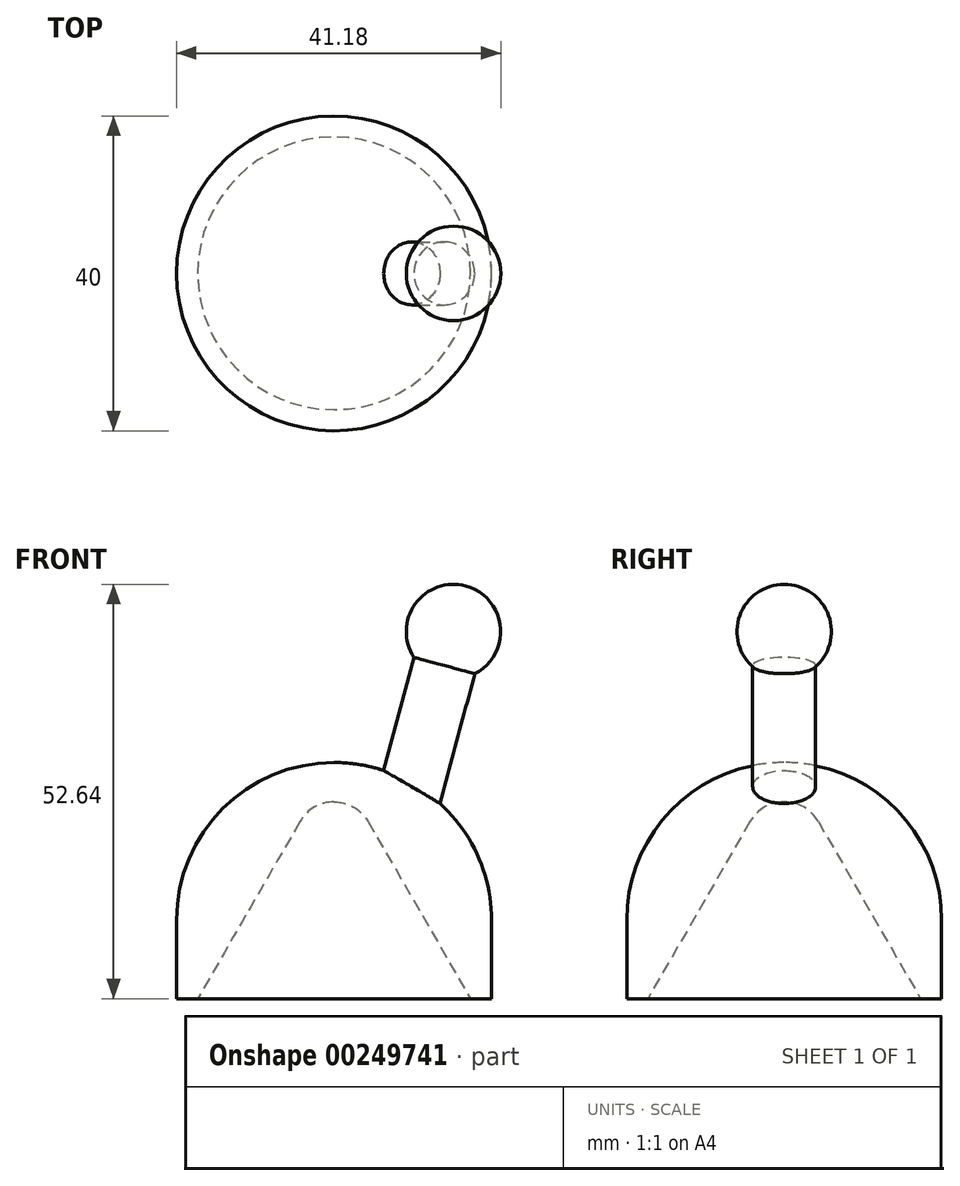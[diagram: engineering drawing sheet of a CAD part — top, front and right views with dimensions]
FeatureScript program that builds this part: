
annotation { "Feature Type Name" : "Feature", "Feature Type Description" : "" }
export const myFeature = defineFeature(function(context is Context, id is Id, definition is map)
    precondition{}
    {
        {
            var Q0;
            Q0=qCreatedBy(makeId("Front.planeOp"),FACE);
            var sketch = newSketch(context, id + "F0", { "sketchPlane" : qUnion([Q0])});
            skArc(sketch, "E0", {"start": v(4.33, 22.5) * mm, "mid": v(2.5, 24.33) * mm, "end": v(0, 25) * mm});
            skLineSegment(sketch, "E1", {"start": v(4.33, 22.5) * mm, "end": v(17.32, 0) * mm});
            skLineSegment(sketch, "E2", {"start": v(17.32, 0) * mm, "end": v(20, 0) * mm});
            skLineSegment(sketch, "E3", {"start": v(20, 0) * mm, "end": v(20, 10) * mm});
            skLineSegment(sketch, "E4", {"start": v(0, 0) * mm, "end": v(0, 30) * mm, "construction": true});
            skArc(sketch, "E5", {"start": v(20, 10) * mm, "mid": v(14.14, 24.14) * mm, "end": v(0, 30) * mm});
            skLineSegment(sketch, "E6", {"start": v(0, 25) * mm, "end": v(0, 30) * mm});
            skSolve(sketch);
        }
        {
            var Q0;
            Q0=makeQuery(id+"F0.imprint","IMPRINT",FACE,{"disambiguationData":[TD([[makeQuery(id+"F0.imprint","IMPRINT",EDGE,{"derivedFrom":sQuery(id+"F0.wireOp",EDGE,"E0")}),-1.0]])]});
            var Q1;
            Q1=sQuery(id+"F0.wireOp",EDGE,"E4");
            revolve(context, id + "F1", {"entities" : qUnion([Q0]), "axis" : qUnion([Q1]), "revolveType" : RevolveType.FULL});
        }
        {
            var Q0;
            Q0=qCreatedBy(makeId("Front.planeOp"),FACE);
            var sketch = newSketch(context, id + "F2", { "sketchPlane" : qUnion([Q0])});
            skArc(sketch, "E7", {"start": v(20, 10) * mm, "mid": v(0, 30) * mm, "end": v(-20, 10) * mm, "construction": true});
            skLineSegment(sketch, "E8", {"start": v(2.68, 0) * mm, "end": v(15.18, 46.64) * mm, "construction": true});
            skPoint(sketch, "E9", {"position": v(10, 27.32) * mm});
            skLineSegment(sketch, "E10", {"start": v(9.3, 24.73) * mm, "end": v(13.17, 23.7) * mm});
            skLineSegment(sketch, "E11", {"start": v(13.17, 23.7) * mm, "end": v(17.88, 41.28) * mm});
            skArc(sketch, "E12", {"start": v(17.88, 41.28) * mm, "mid": v(21.14, 47.26) * mm, "end": v(16.73, 52.43) * mm});
            skLineSegment(sketch, "E13", {"start": v(15.18, 46.64) * mm, "end": v(16.73, 52.43) * mm});
            skLineSegment(sketch, "E14", {"start": v(15.18, 46.64) * mm, "end": v(9.3, 24.73) * mm});
            skSolve(sketch);
        }
        {
            var Q0;
            Q0=makeQuery(id+"F2.imprint","IMPRINT",FACE,{"disambiguationData":[TD([[makeQuery(id+"F2.imprint","IMPRINT",EDGE,{"derivedFrom":sQuery(id+"F2.wireOp",EDGE,"E10")}),1.0]])]});
            var Q1;
            Q1=sQuery(id+"F2.wireOp",EDGE,"E14");
            revolve(context, id + "F3", {"operationType" : NewBodyOperationType.ADD, "entities" : qUnion([Q0]), "axis" : qUnion([Q1]), "revolveType" : RevolveType.FULL});
        }
    });
